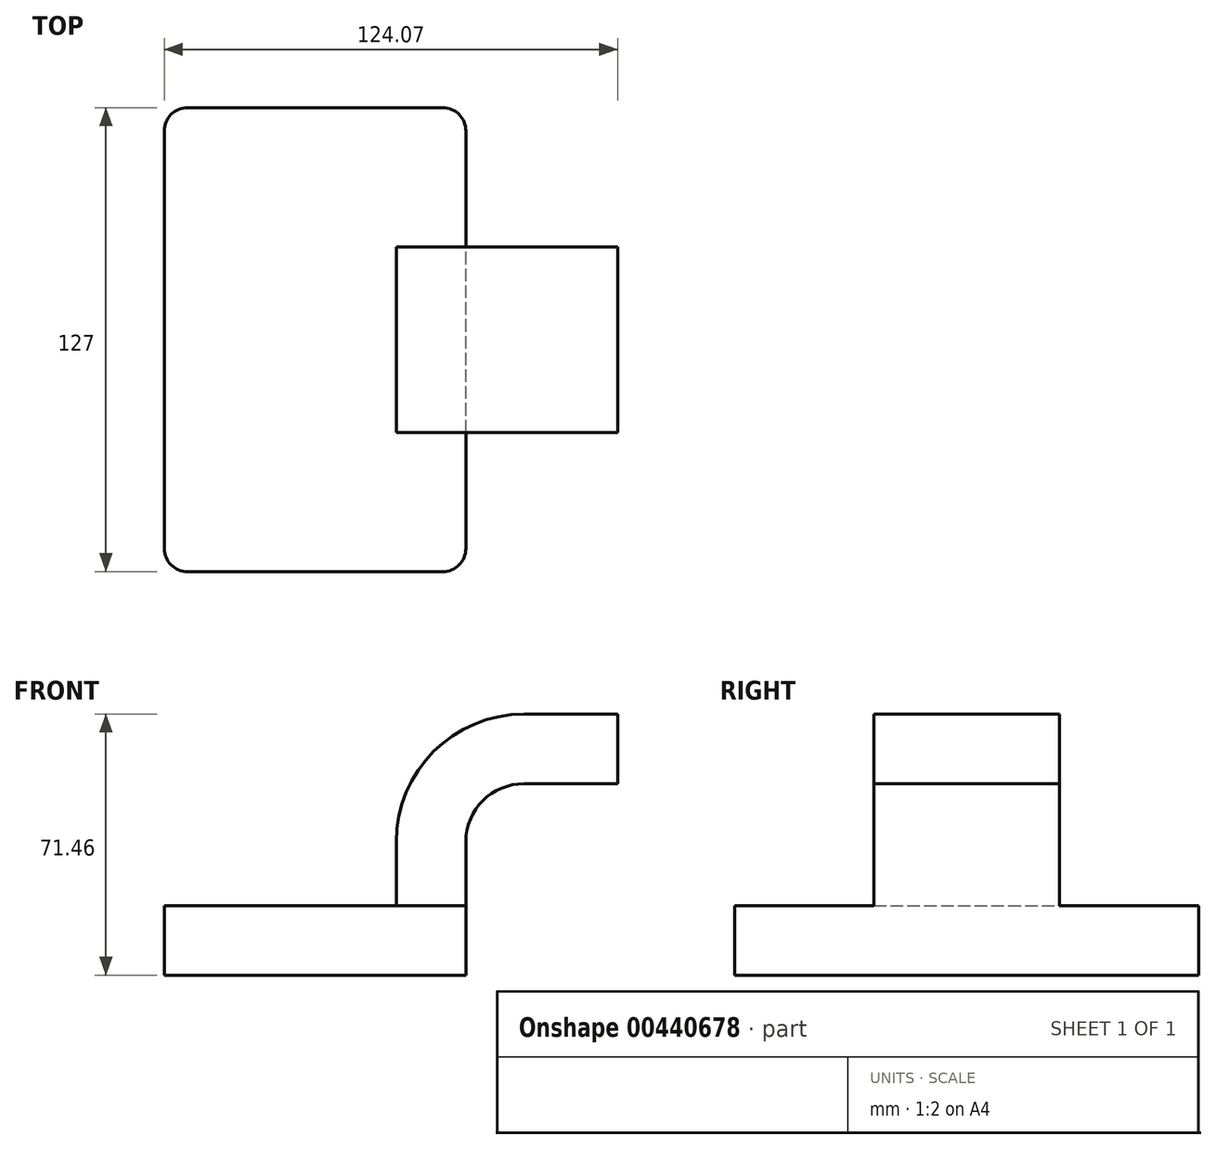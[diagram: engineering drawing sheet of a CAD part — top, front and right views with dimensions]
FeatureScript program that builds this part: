
annotation { "Feature Type Name" : "Feature", "Feature Type Description" : "" }
export const myFeature = defineFeature(function(context is Context, id is Id, definition is map)
    precondition{}
    {
        {
            var Q0;
            Q0=qCreatedBy(makeId("Front.planeOp"),FACE);
            var sketch = newSketch(context, id + "F0", { "sketchPlane" : qUnion([Q0])});
            skLineSegment(sketch, "E0.bottom", {"start": v(-41.28, 9.52) * mm, "end": v(41.28, 9.53) * mm});
            skLineSegment(sketch, "E0.top", {"start": v(-41.28, -9.53) * mm, "end": v(41.28, -9.53) * mm});
            skLineSegment(sketch, "E0.left", {"start": v(-41.28, 9.52) * mm, "end": v(-41.28, -9.53) * mm});
            skLineSegment(sketch, "E0.right", {"start": v(41.28, 9.53) * mm, "end": v(41.28, -9.52) * mm});
            skPoint(sketch, "E0.middle", {"position": v(0, 0) * mm});
            skLineSegment(sketch, "E1.bottom", {"start": v(60.32, 66.68) * mm, "end": v(111.12, 66.68) * mm});
            skLineSegment(sketch, "E1.top", {"start": v(60.32, 38.1) * mm, "end": v(111.12, 38.1) * mm});
            skLineSegment(sketch, "E1.left", {"start": v(60.32, 66.68) * mm, "end": v(60.32, 38.1) * mm});
            skLineSegment(sketch, "E1.right", {"start": v(111.12, 66.68) * mm, "end": v(111.12, 38.1) * mm});
            skPoint(sketch, "E1.middle", {"position": v(85.72, 52.39) * mm});
            skLineSegment(sketch, "E2", {"start": v(41.27, 9.53) * mm, "end": v(41.27, 27) * mm});
            skArc(sketch, "E3", {"start": v(41.27, 27) * mm, "mid": v(45.92, 38.23) * mm, "end": v(57.15, 42.88) * mm});
            skLineSegment(sketch, "E4", {"start": v(57.15, 42.88) * mm, "end": v(82.8, 42.88) * mm});
            skLineSegment(sketch, "E5.0", {"start": v(57.15, 61.93) * mm, "end": v(82.8, 61.93) * mm});
            skArc(sketch, "E5.1", {"start": v(22.22, 27) * mm, "mid": v(32.45, 51.7) * mm, "end": v(57.15, 61.93) * mm});
            skLineSegment(sketch, "E5.2", {"start": v(22.22, 9.53) * mm, "end": v(22.22, 27) * mm});
            skLineSegment(sketch, "E6", {"start": v(82.8, 61.93) * mm, "end": v(82.8, 42.88) * mm});
            skFitSpline(sketch, "E7", {"points": [v(-41.28, 9.52) * mm, v(57.15, 61.93) * mm], "startDerivative": vector(10.7, 97.05) * mm, "endDerivative": vector(65.88, -21.17) * mm});
            skSolve(sketch);
        }
        {
            var Q0;
            Q0=makeQuery(id+"F0.imprint","IMPRINT",FACE,{"disambiguationData":[TD([[makeQuery(id+"F0.imprint","IMPRINT",EDGE,{"derivedFrom":sQuery(id+"F0.wireOp",EDGE,"E0.top")}),1.0]])]});
            extrude(context, id + "F1", {"entities" : qUnion([Q0]), "endBound" : BoundingType.SYMMETRIC, "depth" : 127 * mm});
        }
        {
            var Q0;
            {var subQ1=sQuery(id+"F0.wireOp",EDGE,"E2");Q0=makeQuery(id+"F0.imprint","IMPRINT",FACE,{"disambiguationData":[TD([[makeQuery(id+"F0.imprint","IMPRINT",EDGE,{"derivedFrom":subQ1}),1.0]])]});}
            var Q1;
            {var subQ5=sQuery(id+"F0.wireOp",EDGE,"E6");Q1=makeQuery(id+"F0.imprint","IMPRINT",FACE,{"disambiguationData":[TD([[makeQuery(id+"F0.imprint","IMPRINT",EDGE,{"derivedFrom":subQ5}),-1.0]])]});}
            extrude(context, id + "F2", {"entities" : qUnion([Q0, Q1]), "operationType" : NewBodyOperationType.ADD, "endBound" : BoundingType.SYMMETRIC, "depth" : 50.8 * mm});
        }
        {
            var Q0;
            Q0=makeQuery(id+"F0.imprint","IMPRINT",FACE,{"disambiguationData":[TD([[makeQuery(id+"F0.imprint","IMPRINT",EDGE,{"derivedFrom":sQuery(id+"F0.wireOp",EDGE,"E5.1")}),1.0]])]});
            extrude(context, id + "F3", {"entities" : qUnion([Q0]), "operationType" : NewBodyOperationType.ADD, "depth" : 15.88 * mm});
        }
        {
            var Q0;
            {var subQ4=sQuery(id+"F0.wireOp",EDGE,"E1.bottom");Q0=makeQuery(id+"F0.imprint","IMPRINT",FACE,{"disambiguationData":[TD([[makeQuery(id+"F0.imprint","IMPRINT",EDGE,{"derivedFrom":subQ4}),-1.0]])]});}
            var Q1;
            Q1=makeQuery(id+"F2.opExtrude","CAP_EDGE",EDGE,{"disambiguationData":[OSD([sQuery(id+"F0.wireOp",EDGE,"E6")])],"isStart":true});
            var Q2;
            Q2=sQuery(id+"F0.wireOp",EDGE,"E6");
            revolve(context, id + "F4", {"bodyType" : ToolBodyType.SURFACE, "operationType" : NewBodyOperationType.INTERSECT, "entities" : qUnion([Q0]), "surfaceEntities" : qUnion([Q1]), "axis" : qUnion([Q2]), "revolveType" : RevolveType.FULL});
        }
        {
            var Q0;
            Q0=makeQuery(id+"F1.opExtrude","CAP_EDGE",EDGE,{"disambiguationData":[OSD([sQuery(id+"F0.wireOp",EDGE,"E0.right")])],"isStart":false});
            var Q1;
            Q1=makeQuery(id+"F1.opExtrude","CAP_EDGE",EDGE,{"disambiguationData":[OSD([sQuery(id+"F0.wireOp",EDGE,"E0.left")])],"isStart":false});
            var Q2;
            Q2=makeQuery(id+"F1.opExtrude","CAP_EDGE",EDGE,{"disambiguationData":[OSD([sQuery(id+"F0.wireOp",EDGE,"E0.left")])],"isStart":true});
            var Q3;
            Q3=makeQuery(id+"F1.opExtrude","CAP_EDGE",EDGE,{"disambiguationData":[OSD([sQuery(id+"F0.wireOp",EDGE,"E0.right")])],"isStart":true});
            fillet(context, id + "F5", {"entities" : qUnion([Q0, Q1, Q2, Q3]), "radius" : 6.35 * mm, "tangentPropagation" : true, "allowEdgeOverflow" : false});
        }
    });
